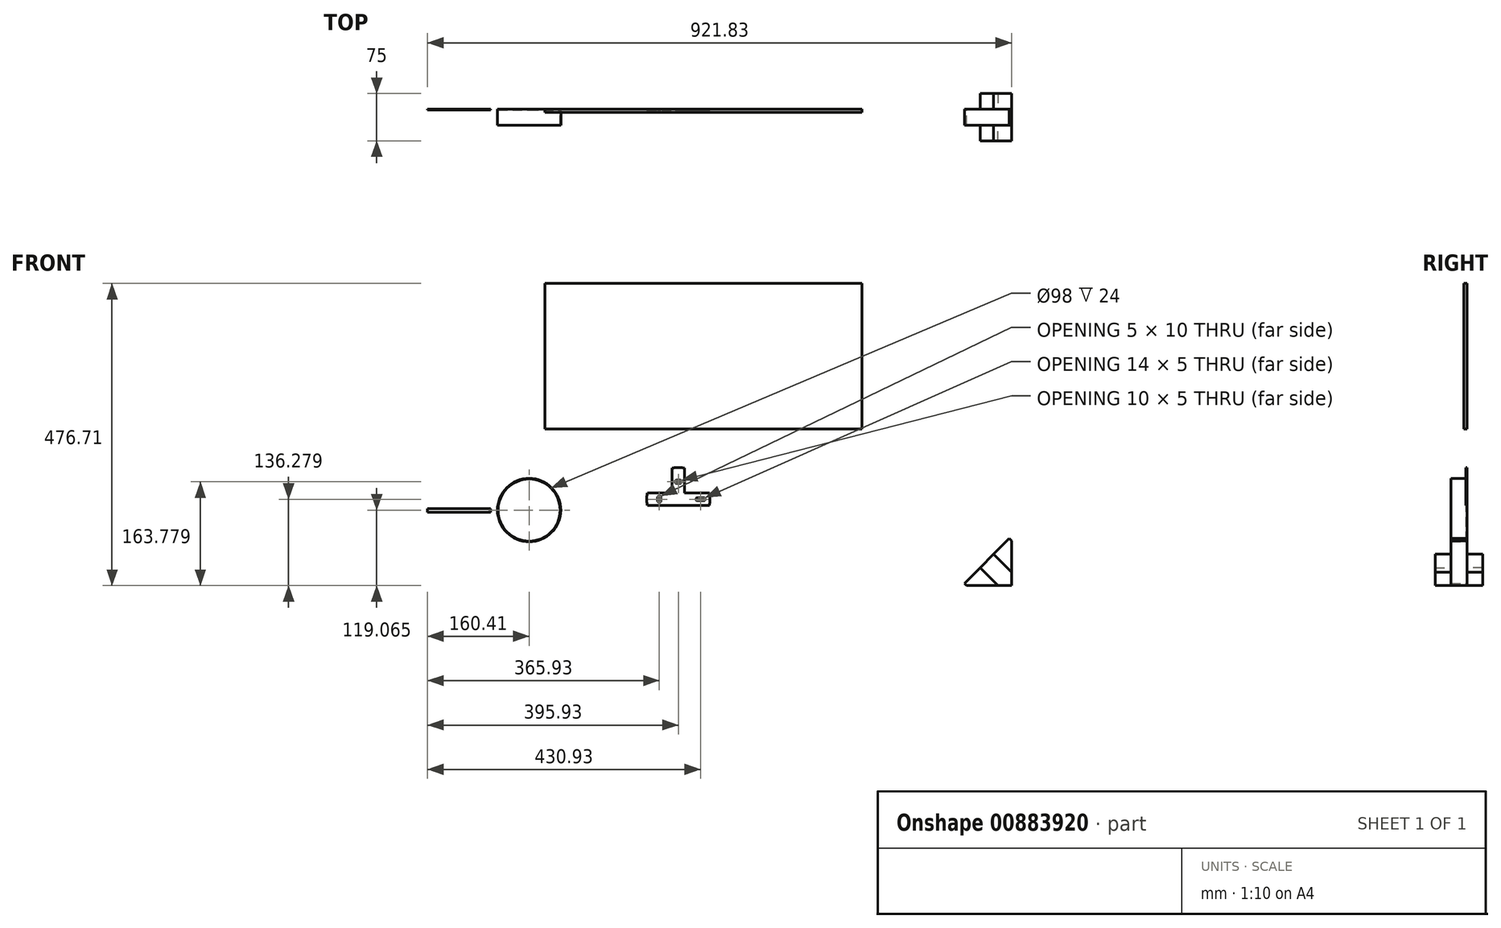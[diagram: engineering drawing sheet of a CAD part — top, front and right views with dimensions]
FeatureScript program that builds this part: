
annotation { "Feature Type Name" : "Feature", "Feature Type Description" : "" }
export const myFeature = defineFeature(function(context is Context, id is Id, definition is map)
    precondition{}
    {
        {
            var Q0;
            Q0=qCreatedBy(makeId("Front.planeOp"),FACE);
            var sketch = newSketch(context, id + "F0", { "sketchPlane" : qUnion([Q0])});
            skCircle(sketch, "E0", {"center": v(0, 0.35) * mm, "radius": 50 * mm});
            skLineSegment(sketch, "E1", {"start": v(-60.55, 2.9) * mm, "end": v(-160.4, 2.9) * mm});
            skLineSegment(sketch, "E2", {"start": v(-160.37, -3.1) * mm, "end": v(-60.59, -3.1) * mm});
            skLineSegment(sketch, "E3", {"start": v(-160.4, 2.9) * mm, "end": v(-160.37, -3.1) * mm});
            skLineSegment(sketch, "E4", {"start": v(-60.55, 2.9) * mm, "end": v(-60.59, -3.1) * mm});
            skSolve(sketch);
        }
        {
            var Q0;
            Q0=makeQuery(id+"F0.imprint","IMPRINT",FACE,{"disambiguationData":[TD([[makeQuery(id+"F0.imprint","IMPRINT",EDGE,{"derivedFrom":sQuery(id+"F0.wireOp",EDGE,"E0")}),1.0]])]});
            extrude(context, id + "F1", {"entities" : qUnion([Q0]), "depth" : 25 * mm, "offsetDistance" : 25 * mm});
        }
        {
            var Q0;
            Q0=makeQuery(id+"F1.opExtrude","CAP_FACE",FACE,{"disambiguationData":[OSD([sQuery(id+"F0.wireOp",EDGE,"E0")])],"isStart":false});
            shell(context, id + "F2", {"entities" : qUnion([Q0]), "thickness" : 1 * mm});
        }
        {
            var Q0;
            Q0=makeQuery(id+"F0.imprint","IMPRINT",FACE,{"disambiguationData":[TD([[makeQuery(id+"F0.imprint","IMPRINT",EDGE,{"derivedFrom":sQuery(id+"F0.wireOp",EDGE,"E1")}),1.0]])]});
            extrude(context, id + "F3", {"entities" : qUnion([Q0]), "depth" : 1 * mm, "offsetDistance" : 25 * mm});
        }
        {
            var Q0;
            Q0=qCreatedBy(makeId("Front.planeOp"),FACE);
            var sketch = newSketch(context, id + "F4", { "sketchPlane" : qUnion([Q0])});
            skArc(sketch, "E5", {"start": v(186.53, 27.56) * mm, "mid": v(185.52, 17.56) * mm, "end": v(186.53, 7.56) * mm});
            skLineSegment(sketch, "E6", {"start": v(186.53, 27.56) * mm, "end": v(225.52, 27.56) * mm});
            skLineSegment(sketch, "E7", {"start": v(186.53, 7.56) * mm, "end": v(284.51, 7.56) * mm});
            skArc(sketch, "E8.trimOffspring", {"start": v(284.51, 7.56) * mm, "mid": v(285.52, 17.56) * mm, "end": v(284.51, 27.56) * mm});
            skLineSegment(sketch, "E9", {"start": v(225.52, 27.56) * mm, "end": v(225.52, 66.55) * mm});
            skLineSegment(sketch, "E10", {"start": v(245.52, 27.56) * mm, "end": v(245.52, 66.55) * mm});
            skLineSegment(sketch, "E11", {"start": v(235.52, 67.56) * mm, "end": v(235.52, 74.08) * mm, "construction": true});
            skArc(sketch, "E12.trimOffspring", {"start": v(245.52, 66.55) * mm, "mid": v(235.52, 67.56) * mm, "end": v(225.52, 66.55) * mm});
            skLineSegment(sketch, "E13.trimOffspring", {"start": v(245.52, 27.56) * mm, "end": v(284.51, 27.56) * mm});
            skLineSegment(sketch, "E14", {"start": v(235.52, 17.56) * mm, "end": v(174.59, 17.56) * mm, "construction": true});
            skLineSegment(sketch, "E15.bottom", {"start": v(205.02, 22.56) * mm, "end": v(205.52, 22.56) * mm});
            skLineSegment(sketch, "E15.top", {"start": v(205.02, 12.56) * mm, "end": v(205.52, 12.56) * mm});
            skLineSegment(sketch, "E16", {"start": v(203.02, 20.56) * mm, "end": v(203.02, 14.56) * mm});
            skLineSegment(sketch, "E17.MirrorCS", {"start": v(206.02, 12.56) * mm, "end": v(205.52, 12.56) * mm});
            skLineSegment(sketch, "E18.MirrorCS", {"start": v(206.02, 22.56) * mm, "end": v(205.52, 22.56) * mm});
            skLineSegment(sketch, "E19.MirrorCS", {"start": v(208.02, 20.56) * mm, "end": v(208.02, 14.56) * mm});
            skPoint(sketch, "E20.visualSharp", {"position": v(203.02, 22.56) * mm});
            skArc(sketch, "E20.filletArc", {"start": v(205.02, 22.56) * mm, "mid": v(203.6, 21.97) * mm, "end": v(203.02, 20.56) * mm});
            skPoint(sketch, "E21.visualSharp", {"position": v(208.02, 22.56) * mm});
            skArc(sketch, "E21.filletArc", {"start": v(208.02, 20.56) * mm, "mid": v(207.43, 21.97) * mm, "end": v(206.02, 22.56) * mm});
            skPoint(sketch, "E22.visualSharp", {"position": v(208.02, 12.56) * mm});
            skArc(sketch, "E22.filletArc", {"start": v(206.02, 12.56) * mm, "mid": v(207.43, 13.14) * mm, "end": v(208.02, 14.56) * mm});
            skPoint(sketch, "E23.visualSharp", {"position": v(203.02, 12.56) * mm});
            skArc(sketch, "E23.filletArc", {"start": v(203.02, 14.56) * mm, "mid": v(203.6, 13.14) * mm, "end": v(205.02, 12.56) * mm});
            skLineSegment(sketch, "E24", {"start": v(270.52, 45.77) * mm, "end": v(270.52, -22.93) * mm, "construction": true});
            skLineSegment(sketch, "E25", {"start": v(235.52, 17.56) * mm, "end": v(307.05, 17.56) * mm, "construction": true});
            skLineSegment(sketch, "E26.bottom", {"start": v(277.52, 18.06) * mm, "end": v(277.52, 17.56) * mm});
            skLineSegment(sketch, "E26.top", {"start": v(263.52, 18.06) * mm, "end": v(263.52, 17.56) * mm});
            skLineSegment(sketch, "E27", {"start": v(275.52, 20.06) * mm, "end": v(265.52, 20.06) * mm});
            skLineSegment(sketch, "E28.MirrorCS", {"start": v(275.52, 15.06) * mm, "end": v(265.52, 15.06) * mm});
            skPoint(sketch, "E29.visualSharp", {"position": v(277.52, 20.06) * mm});
            skArc(sketch, "E29.filletArc", {"start": v(277.52, 18.06) * mm, "mid": v(276.93, 19.47) * mm, "end": v(275.52, 20.06) * mm});
            skPoint(sketch, "E30.visualSharp", {"position": v(275.46, 15.06) * mm});
            skArc(sketch, "E30.filletArc", {"start": v(275.52, 15.06) * mm, "mid": v(276.93, 15.64) * mm, "end": v(277.52, 17.06) * mm});
            skPoint(sketch, "E31.visualSharp", {"position": v(265.46, 15.06) * mm});
            skArc(sketch, "E31.filletArc", {"start": v(263.52, 17.06) * mm, "mid": v(264.1, 15.64) * mm, "end": v(265.52, 15.06) * mm});
            skPoint(sketch, "E32.visualSharp", {"position": v(263.52, 20.06) * mm});
            skArc(sketch, "E32.filletArc", {"start": v(265.52, 20.06) * mm, "mid": v(264.1, 19.47) * mm, "end": v(263.52, 18.06) * mm});
            skLineSegment(sketch, "E33", {"start": v(263.52, 17.06) * mm, "end": v(263.52, 17.56) * mm});
            skLineSegment(sketch, "E34", {"start": v(277.52, 17.06) * mm, "end": v(277.52, 17.56) * mm});
            skLineSegment(sketch, "E35", {"start": v(238.52, 47.56) * mm, "end": v(232.52, 47.56) * mm});
            skLineSegment(sketch, "E36.MirrorCS", {"start": v(230.52, 44.56) * mm, "end": v(230.52, 45.06) * mm});
            skLineSegment(sketch, "E37.MirrorCS", {"start": v(240.52, 44.56) * mm, "end": v(240.52, 45.06) * mm});
            skLineSegment(sketch, "E38.MirrorCS", {"start": v(238.52, 42.56) * mm, "end": v(232.52, 42.56) * mm});
            skPoint(sketch, "E39.visualSharp", {"position": v(240.52, 47.56) * mm});
            skArc(sketch, "E39.filletArc", {"start": v(240.52, 45.56) * mm, "mid": v(239.93, 46.97) * mm, "end": v(238.52, 47.56) * mm});
            skPoint(sketch, "E40.visualSharp", {"position": v(240.52, 42.56) * mm});
            skArc(sketch, "E40.filletArc", {"start": v(238.52, 42.56) * mm, "mid": v(239.93, 43.14) * mm, "end": v(240.52, 44.56) * mm});
            skPoint(sketch, "E41.visualSharp", {"position": v(230.52, 42.56) * mm});
            skArc(sketch, "E41.filletArc", {"start": v(230.52, 44.56) * mm, "mid": v(231.1, 43.14) * mm, "end": v(232.52, 42.56) * mm});
            skPoint(sketch, "E42.visualSharp", {"position": v(230.52, 47.56) * mm});
            skArc(sketch, "E42.filletArc", {"start": v(232.52, 47.56) * mm, "mid": v(231.1, 46.97) * mm, "end": v(230.52, 45.56) * mm});
            skLineSegment(sketch, "E43", {"start": v(235.52, 17.56) * mm, "end": v(235.52, 89.44) * mm, "construction": true});
            skPoint(sketch, "E43.endSnap0", {"position": v(235.52, 70.82) * mm});
            skLineSegment(sketch, "E44", {"start": v(240.52, 45.56) * mm, "end": v(240.52, 45.06) * mm});
            skLineSegment(sketch, "E45", {"start": v(230.52, 45.56) * mm, "end": v(230.52, 45.06) * mm});
            skCircle(sketch, "E46", {"center": v(235.52, 17.56) * mm, "radius": 50 * mm});
            skLineSegment(sketch, "E47.bottom", {"start": v(24.8, 357.99) * mm, "end": v(525.48, 357.99) * mm});
            skLineSegment(sketch, "E47.top", {"start": v(24.8, 128.2) * mm, "end": v(525.48, 128.2) * mm});
            skLineSegment(sketch, "E47.left", {"start": v(24.8, 357.99) * mm, "end": v(24.8, 128.2) * mm});
            skLineSegment(sketch, "E47.right", {"start": v(525.48, 357.99) * mm, "end": v(525.48, 128.2) * mm});
            skLineSegment(sketch, "E48", {"start": v(761.42, -48) * mm, "end": v(761.42, -118.72) * mm});
            skLineSegment(sketch, "E49", {"start": v(761.42, -118.72) * mm, "end": v(690.71, -118.72) * mm});
            skLineSegment(sketch, "E50", {"start": v(761.42, -48) * mm, "end": v(690.71, -118.72) * mm});
            skSolve(sketch);
        }
        {
            var Q0;
            {var subQ3=sQuery(id+"F4.wireOp",EDGE,"E6");Q0=makeQuery(id+"F4.imprint","IMPRINT",FACE,{"disambiguationData":[TD([[makeQuery(id+"F4.imprint","IMPRINT",EDGE,{"derivedFrom":subQ3}),-1.0]])]});}
            extrude(context, id + "F5", {"entities" : qUnion([Q0]), "depth" : 1.5 * mm, "offsetDistance" : 25 * mm});
        }
        {
            var Q0;
            Q0=sQuery(id+"F4.wireOp",EDGE,"E46");
            extrude(context, id + "F6", {"bodyType" : ToolBodyType.SURFACE, "surfaceEntities" : qUnion([Q0]), "depth" : 1.5 * mm, "offsetDistance" : 25 * mm});
        }
        {
            var Q0;
            Q0=makeQuery(id+"F4.imprint","IMPRINT",FACE,{"disambiguationData":[TD([[makeQuery(id+"F4.imprint","IMPRINT",EDGE,{"derivedFrom":sQuery(id+"F4.wireOp",EDGE,"E47.bottom")}),-1.0]])]});
            extrude(context, id + "F7", {"entities" : qUnion([Q0]), "depth" : 5 * mm, "offsetDistance" : 25 * mm});
        }
        {
            var Q0;
            Q0=makeQuery(id+"F4.imprint","IMPRINT",FACE,{"disambiguationData":[TD([[makeQuery(id+"F4.imprint","IMPRINT",EDGE,{"derivedFrom":sQuery(id+"F4.wireOp",EDGE,"E48")}),-1.0]])]});
            extrude(context, id + "F8", {"entities" : qUnion([Q0]), "depth" : 25 * mm, "offsetDistance" : 25 * mm});
        }
        {
            var Q0;
            Q0=makeQuery(id+"F8.opExtrude","SWEPT_FACE",FACE,{"disambiguationData":[OSD([sQuery(id+"F4.wireOp",EDGE,"E50")])]});
            var sketch = newSketch(context, id + "F9", { "sketchPlane" : qUnion([Q0])});
            skSolve(sketch);
        }
        {
            var Q0;
            {var subQ0=sQuery(id+"F4.wireOp",EDGE,"E50");Q0=makeQuery(id+"F9.imprint","IMPRINT",FACE,{"disambiguationData":[TD([[makeQuery(id+"F9.imprint","IMPRINT",EDGE,{"derivedFrom":makeQuery(id+"F8.opExtrude","CAP_EDGE",EDGE,{"disambiguationData":[OSD([subQ0])],"isStart":true})}),1.0]])]});}
            var sketch = newSketch(context, id + "F10", { "sketchPlane" : qUnion([Q0])});
            skSolve(sketch);
        }
        {
            var Q0;
            Q0 = qSketchRegion(id + "F10", true);
            var Q1;
            {var subQ0=sQuery(id+"F4.wireOp",EDGE,"E50");Q1=makeQuery(id+"F9.imprint","IMPRINT",FACE,{"disambiguationData":[TD([[makeQuery(id+"F9.imprint","IMPRINT",EDGE,{"derivedFrom":makeQuery(id+"F8.opExtrude","CAP_EDGE",EDGE,{"disambiguationData":[OSD([subQ0])],"isStart":true})}),1.0]])]});}
            extrude(context, id + "F11", {"entities" : qUnion([Q0, Q1]), "operationType" : NewBodyOperationType.ADD, "depth" : 5 * mm, "offsetDistance" : 25 * mm});
        }
        {
            var Q0;
            Q0=qCreatedBy(makeId("Front.planeOp"),FACE);
            var sketch = newSketch(context, id + "F12", { "sketchPlane" : qUnion([Q0])});
            skLineSegment(sketch, "E51", {"start": v(761.42, -97.5) * mm, "end": v(733.14, -69.22) * mm});
            skLineSegment(sketch, "E52", {"start": v(733.14, -69.22) * mm, "end": v(711.92, -90.44) * mm});
            skLineSegment(sketch, "E53", {"start": v(711.92, -90.44) * mm, "end": v(740.2, -118.72) * mm});
            skLineSegment(sketch, "E54", {"start": v(761.42, -118.72) * mm, "end": v(678.3, -35.6) * mm, "construction": true});
            skLineSegment(sketch, "E55", {"start": v(761.42, -97.5) * mm, "end": v(761.42, -118.72) * mm});
            skLineSegment(sketch, "E56", {"start": v(740.2, -118.72) * mm, "end": v(761.42, -118.72) * mm});
            skSolve(sketch);
        }
        {
            var Q0;
            Q0=makeQuery(id+"F12.imprint","IMPRINT",FACE,{"disambiguationData":[TD([[makeQuery(id+"F12.imprint","IMPRINT",EDGE,{"derivedFrom":sQuery(id+"F12.wireOp",EDGE,"E51")}),1.0]])]});
            extrude(context, id + "F13", {"entities" : qUnion([Q0]), "oppositeDirection" : true, "depth" : 25 * mm, "offsetDistance" : 25 * mm});
        }
        {
            var Q0;
            Q0=makeQuery(id+"F8.opExtrude","CAP_FACE",FACE,{"disambiguationData":[OSD([sQuery(id+"F4.wireOp",EDGE,"E48"),sQuery(id+"F4.wireOp",EDGE,"E49"),sQuery(id+"F4.wireOp",EDGE,"E50")])],"isStart":false});
            var sketch = newSketch(context, id + "F14", { "sketchPlane" : qUnion([Q0])});
            skLineSegment(sketch, "E57", {"start": v(761.42, -97.5) * mm, "end": v(733.14, -69.22) * mm});
            skLineSegment(sketch, "E58", {"start": v(733.14, -69.22) * mm, "end": v(711.92, -90.44) * mm});
            skLineSegment(sketch, "E59", {"start": v(711.92, -90.44) * mm, "end": v(740.2, -118.72) * mm});
            skLineSegment(sketch, "E60", {"start": v(761.42, -118.72) * mm, "end": v(678.3, -35.6) * mm, "construction": true});
            skLineSegment(sketch, "E61", {"start": v(761.42, -97.5) * mm, "end": v(761.42, -118.72) * mm});
            skLineSegment(sketch, "E62", {"start": v(740.2, -118.72) * mm, "end": v(761.42, -118.72) * mm});
            skSolve(sketch);
        }
        {
            var Q0;
            {var subQ4=sQuery(id+"F14.wireOp",EDGE,"E61");Q0=makeQuery(id+"F14.imprint","IMPRINT",FACE,{"disambiguationData":[TD([[makeQuery(id+"F14.imprint","IMPRINT",EDGE,{"derivedFrom":subQ4}),-1.0]])]});}
            var Q1;
            {var subQ0=sQuery(id+"F14.wireOp",EDGE,"E58");Q1=makeQuery(id+"F14.imprint","IMPRINT",FACE,{"disambiguationData":[TD([[makeQuery(id+"F14.imprint","IMPRINT",EDGE,{"derivedFrom":subQ0}),1.0]])]});}
            extrude(context, id + "F15", {"entities" : qUnion([Q0, Q1]), "depth" : 25 * mm, "offsetDistance" : 25 * mm});
        }
    });
